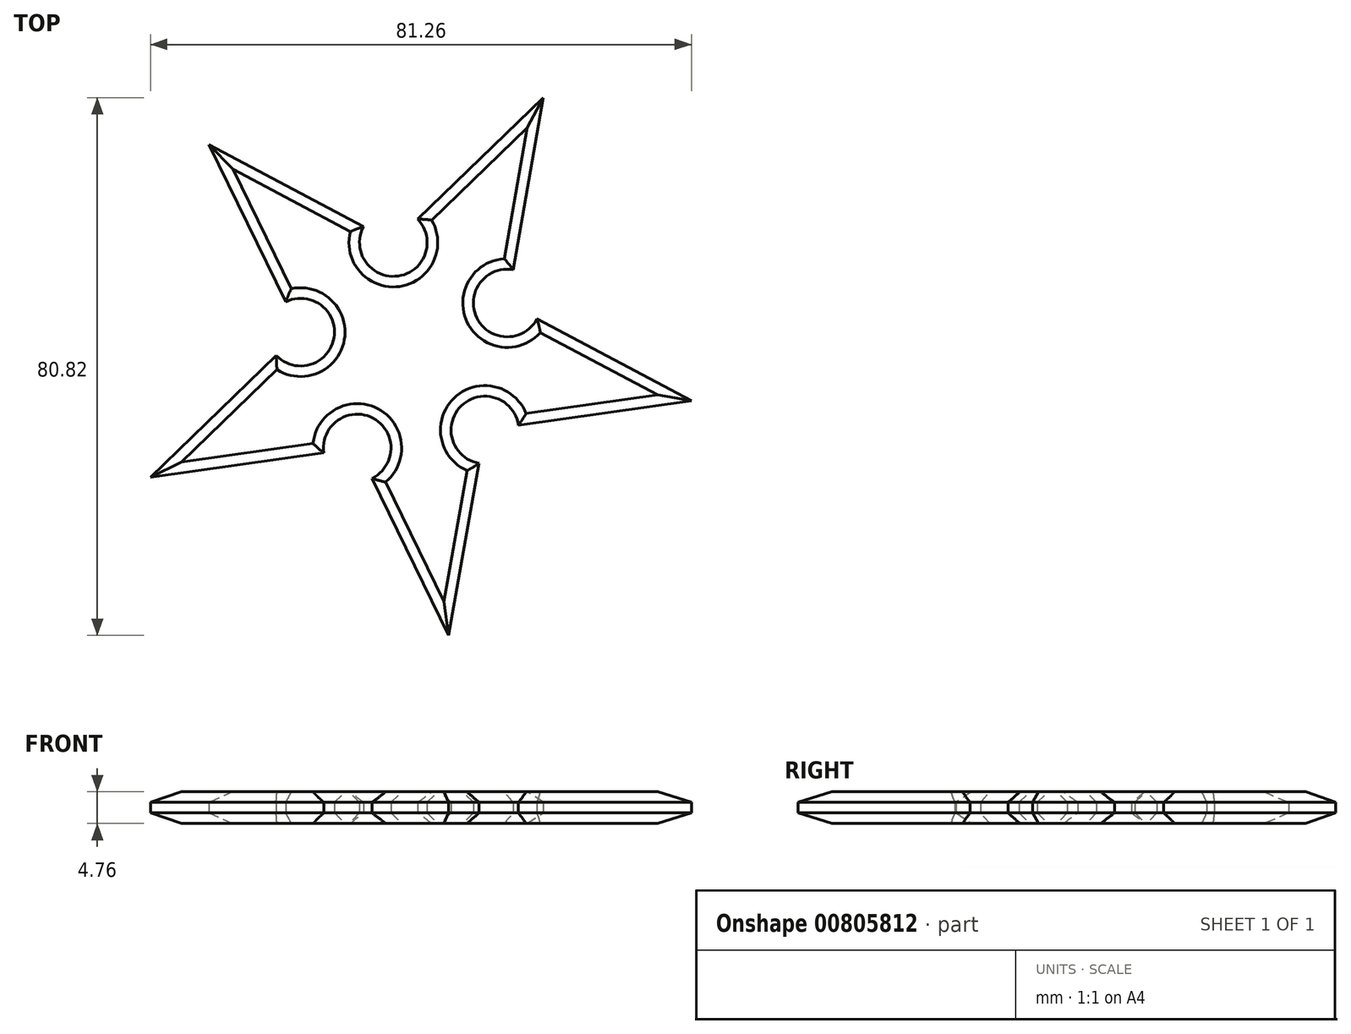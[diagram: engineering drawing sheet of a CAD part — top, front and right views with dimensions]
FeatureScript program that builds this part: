
annotation { "Feature Type Name" : "Feature", "Feature Type Description" : "" }
export const myFeature = defineFeature(function(context is Context, id is Id, definition is map)
    precondition{}
    {
        {
            var Q0;
            Q0=qCreatedBy(makeId("Top.planeOp"),FACE);
            var sketch = newSketch(context, id + "F0", { "sketchPlane" : qUnion([Q0])});
            skPoint(sketch, "E0.0.midPoint", {"position": v(31.36, 15.31) * mm});
            skLineSegment(sketch, "E1", {"start": v(-29.98, 31.02) * mm, "end": v(-18.46, 7.42) * mm});
            skLineSegment(sketch, "E2", {"start": v(20.24, 38.1) * mm, "end": v(15.69, 12.23) * mm});
            skLineSegment(sketch, "E3", {"start": v(-38.77, -18.93) * mm, "end": v(-12.76, -15.26) * mm});
            skLineSegment(sketch, "E4", {"start": v(-29.98, 31.02) * mm, "end": v(-6.79, 18.7) * mm});
            skLineSegment(sketch, "E5", {"start": v(-38.77, -18.93) * mm, "end": v(-19.88, -0.68) * mm});
            skLineSegment(sketch, "E6.trimOffspring", {"start": v(1.35, 19.85) * mm, "end": v(20.24, 38.1) * mm});
            skLineSegment(sketch, "E7.trimOffspring", {"start": v(-5.5, -19.12) * mm, "end": v(6.02, -42.72) * mm});
            skLineSegment(sketch, "E8.trimOffspring", {"start": v(19.3, 4.85) * mm, "end": v(42.49, -7.47) * mm});
            skLineSegment(sketch, "E9.trimOffspring", {"start": v(10.57, -16.85) * mm, "end": v(6.02, -42.72) * mm});
            skLineSegment(sketch, "E10.trimOffspring", {"start": v(16.48, -11.14) * mm, "end": v(42.49, -7.47) * mm});
            skArc(sketch, "E11", {"start": v(-6.79, 18.7) * mm, "mid": v(-1.6, 11.29) * mm, "end": v(1.35, 19.85) * mm});
            skArc(sketch, "E12", {"start": v(-19.88, -0.68) * mm, "mid": v(-11.23, 1.97) * mm, "end": v(-18.46, 7.42) * mm});
            skArc(sketch, "E13", {"start": v(-5.5, -19.12) * mm, "mid": v(-5.35, -10.07) * mm, "end": v(-12.76, -15.26) * mm});
            skArc(sketch, "E14", {"start": v(16.48, -11.14) * mm, "mid": v(7.92, -8.2) * mm, "end": v(10.57, -16.85) * mm});
            skArc(sketch, "E15", {"start": v(15.69, 12.23) * mm, "mid": v(10.24, 5) * mm, "end": v(19.3, 4.85) * mm});
            skPoint(sketch, "E0.cCircle.center.orphan", {"position": v(0, 0) * mm});
            skSolve(sketch);
        }
        {
            var Q0;
            Q0=qSketchRegion(id+"F0",true);
            extrude(context, id + "F1", {"entities" : qUnion([Q0]), "depth" : 4.76 * mm});
        }
        {
            var Q0;
            Q0=makeQuery(id+"F1.opExtrude","CAP_FACE",FACE,{"disambiguationData":[OSD([sQuery(id+"F0.wireOp",EDGE,"E1"),sQuery(id+"F0.wireOp",EDGE,"E2"),sQuery(id+"F0.wireOp",EDGE,"E3"),sQuery(id+"F0.wireOp",EDGE,"E4"),sQuery(id+"F0.wireOp",EDGE,"E5"),sQuery(id+"F0.wireOp",EDGE,"E6.trimOffspring"),sQuery(id+"F0.wireOp",EDGE,"E7.trimOffspring"),sQuery(id+"F0.wireOp",EDGE,"E8.trimOffspring"),sQuery(id+"F0.wireOp",EDGE,"E9.trimOffspring"),sQuery(id+"F0.wireOp",EDGE,"E10.trimOffspring")])],"isStart":false});
            var Q1;
            Q1=makeQuery(id+"F1.opExtrude","CAP_FACE",FACE,{"disambiguationData":[OSD([sQuery(id+"F0.wireOp",EDGE,"E1"),sQuery(id+"F0.wireOp",EDGE,"E2"),sQuery(id+"F0.wireOp",EDGE,"E3"),sQuery(id+"F0.wireOp",EDGE,"E4"),sQuery(id+"F0.wireOp",EDGE,"E5"),sQuery(id+"F0.wireOp",EDGE,"E6.trimOffspring"),sQuery(id+"F0.wireOp",EDGE,"E7.trimOffspring"),sQuery(id+"F0.wireOp",EDGE,"E8.trimOffspring"),sQuery(id+"F0.wireOp",EDGE,"E9.trimOffspring"),sQuery(id+"F0.wireOp",EDGE,"E10.trimOffspring")])],"isStart":true});
            chamfer(context, id + "F2", {"entities" : qUnion([Q0, Q1]), "width" : 1.59 * mm, "tangentPropagation" : true});
        }
    });
